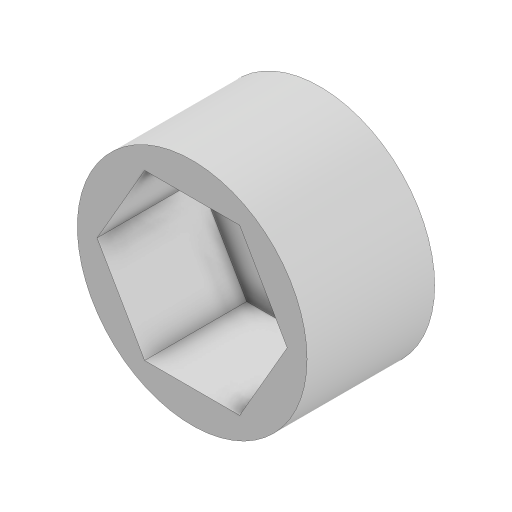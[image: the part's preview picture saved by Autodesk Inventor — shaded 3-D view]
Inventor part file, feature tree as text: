
AUTODESK INVENTOR PART (.ipt)
format: ipt  version: 2023 (Build 270158000, 158)  size: 128,000 bytes
history: native  units: mm
features: extrude x2, sketch x1
ambient origin geometry x8: Origin, YZ Plane, XZ Plane, XY Plane, X Axis, Y Axis, Z Axis, Center Point
bodies: Solid1 (feature_tree)
feature tree (3):
  sketch  "Sketch1"  dims[d0=13.1mm d1=18.0mm d2=4.9mm d3=8.0mm d4=0.0mm d5=2.0mm d6=0.0mm]
  extrude  "Extrusion1"  Depth=2.0mm
  extrude  "Extrusion2"  Depth=2.0mm
